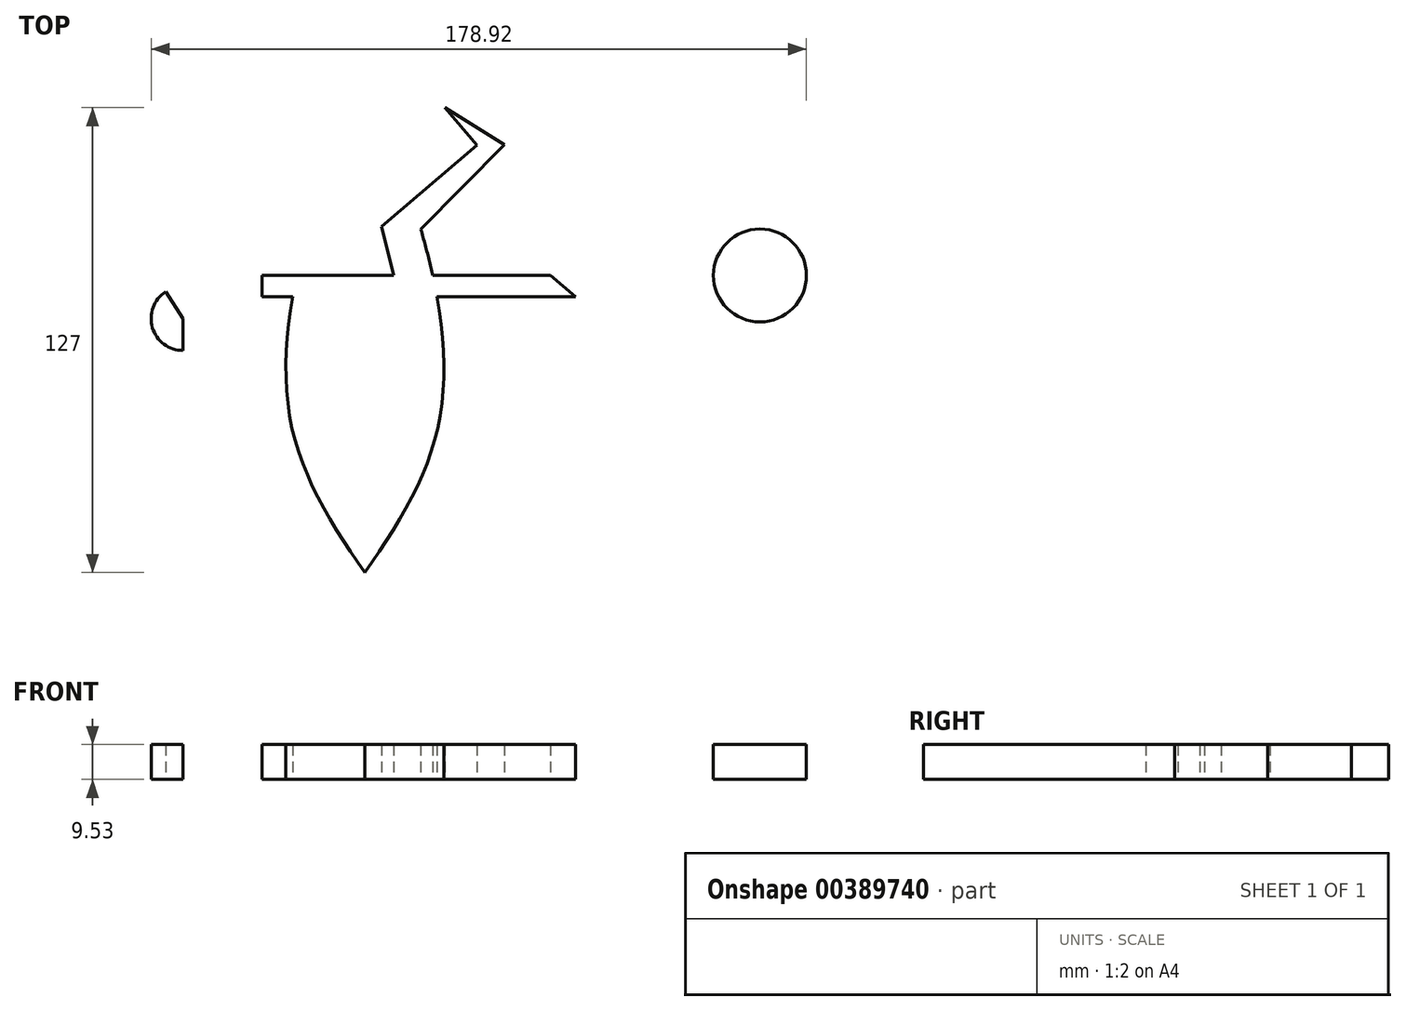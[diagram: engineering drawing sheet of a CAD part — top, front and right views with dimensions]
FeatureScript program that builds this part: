
annotation { "Feature Type Name" : "Feature", "Feature Type Description" : "" }
export const myFeature = defineFeature(function(context is Context, id is Id, definition is map)
    precondition{}
    {
        {
            var Q0;
            Q0=qCreatedBy(makeId("Top.planeOp"),FACE);
            var sketch = newSketch(context, id + "F0", { "sketchPlane" : qUnion([Q0])});
            skLineSegment(sketch, "E0", {"start": v(0, 0) * mm, "end": v(0, 66.19) * mm, "construction": true});
            skFitSpline(sketch, "E1.MirrorCS", {"points": [v(15.27, 31.46) * mm, v(20.14, -21.68) * mm, v(0, -62.35) * mm], "startDerivative": vector(30.92, -106.4) * mm, "endDerivative": vector(-55.93, -80.87) * mm});
            skLineSegment(sketch, "E2", {"start": v(15.27, 31.46) * mm, "end": v(38.1, 54.48) * mm});
            skLineSegment(sketch, "E3", {"start": v(38.1, 54.48) * mm, "end": v(21.8, 64.65) * mm});
            skLineSegment(sketch, "E4", {"start": v(21.8, 64.65) * mm, "end": v(30.54, 54.42) * mm});
            skLineSegment(sketch, "E5", {"start": v(30.54, 54.42) * mm, "end": v(4.54, 32.2) * mm});
            skLineSegment(sketch, "E6", {"start": v(4.54, 32.2) * mm, "end": v(7.8, 18.82) * mm});
            skLineSegment(sketch, "E7", {"start": v(14.96, -10.55) * mm, "end": v(0, -53.14) * mm});
            skLineSegment(sketch, "E8.MirrorCS", {"start": v(-21.8, 64.65) * mm, "end": v(-30.54, 54.42) * mm});
            skLineSegment(sketch, "E9.MirrorCS", {"start": v(-38.1, 54.48) * mm, "end": v(-21.8, 64.65) * mm});
            skLineSegment(sketch, "E10.MirrorCS", {"start": v(-30.54, 54.42) * mm, "end": v(-4.54, 32.2) * mm});
            skLineSegment(sketch, "E11.MirrorCS", {"start": v(-4.54, 32.2) * mm, "end": v(-7.8, 18.82) * mm});
            skPoint(sketch, "E12.MirrorCS.end.orphan", {"position": v(-38.1, 54.48) * mm});
            skPoint(sketch, "E12.MirrorCS.start.orphan", {"position": v(-15.27, 31.46) * mm});
            skPoint(sketch, "E13.MirrorCS.end.orphan", {"position": v(0, -53.14) * mm});
            skPoint(sketch, "E13.MirrorCS.start.orphan", {"position": v(-14.96, -10.55) * mm});
            skLineSegment(sketch, "E14", {"start": v(-37.64, 13.01) * mm, "end": v(57.57, 13.01) * mm});
            skLineSegment(sketch, "E15", {"start": v(57.57, 13.01) * mm, "end": v(50.72, 18.82) * mm});
            skLineSegment(sketch, "E16", {"start": v(50.72, 18.82) * mm, "end": v(-28.13, 18.82) * mm});
            skLineSegment(sketch, "E17", {"start": v(-41.87, 18.82) * mm, "end": v(-37.64, 13.01) * mm});
            skFitSpline(sketch, "E18.trimOffspring", {"points": [v(-15.27, 31.46) * mm, v(-20.14, -21.68) * mm, v(0, -62.35) * mm], "startDerivative": vector(-30.92, -106.4) * mm, "endDerivative": vector(55.93, -80.87) * mm});
            skLineSegment(sketch, "E19.trimOffspring", {"start": v(-9.22, 13.01) * mm, "end": v(-14.96, -10.55) * mm});
            skLineSegment(sketch, "E20.trimOffspring", {"start": v(9.22, 13.01) * mm, "end": v(14.96, -10.55) * mm});
            skArc(sketch, "E21", {"start": v(-54.4, 14.35) * mm, "mid": v(-57.99, 4.56) * mm, "end": v(-49.63, -1.67) * mm});
            skLineSegment(sketch, "E22", {"start": v(-54.4, 14.35) * mm, "end": v(-49.63, 7.05) * mm});
            skLineSegment(sketch, "E23", {"start": v(-49.63, 7.05) * mm, "end": v(-49.63, -1.67) * mm});
            skLineSegment(sketch, "E24", {"start": v(-28.13, 23.13) * mm, "end": v(-28.13, 4.17) * mm});
            skLineSegment(sketch, "E25", {"start": v(50.72, 18.82) * mm, "end": v(107.87, 18.82) * mm, "construction": true});
            skCircle(sketch, "E26", {"center": v(107.87, 18.82) * mm, "radius": 12.7 * mm});
            skSolve(sketch);
        }
        {
            var Q0;
            Q0 = qSketchRegion(id + "F0", true);
            extrude(context, id + "F1", {"entities" : qUnion([Q0]), "depth" : 9.52 * mm});
        }
    });
